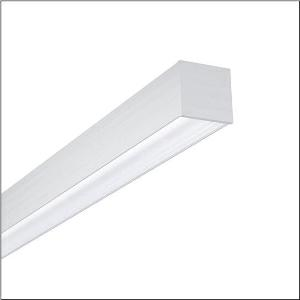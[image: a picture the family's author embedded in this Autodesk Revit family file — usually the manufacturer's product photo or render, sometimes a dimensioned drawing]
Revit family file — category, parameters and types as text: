
# Revit family: silica_r_5mx31bd1e4a_96a8
name_source: partatom
category: Lighting Fixtures
units: mm (PartAtom-declared; Revit-internal decimal feet)

## family parameters
Cut with Voids When Loaded = No
Host = Face
Light Source = No
Part Type = Normal
Room Calculation Point = No
Round Connector Dimension = Use Diameter
Shared = No

## types (1)
- --- (1 x LED, 7070 lm, 45.6 W, 4000K)
    Apparent Load = 46 VA
    CIE Flux Codes = 82 97 100 70 100
    Color Rendering = 80
    Color Temperature = 4000K
    Default Elevation = 1800 mm
    Description = Silica®, office luminaire, of aluminium, light emission: direct/indirect distribution, primary light characteristic: symmetric, installation type: suspended mounting, LED, rated luminous flux: 7.070lm, luminous efficacy: 155lm/W, light colour: 840, colour temperature: 4000K, control gear: ECG DALI, with terminal, 3+2-pole, max. 2.5mm², mains connection: 230V, AC, 50/60Hz, connection cable inclusive, cable length: 1,5m, rated input power: 46W, luminaire housing, of aluminium, anodised, silver, length: 1.442mm, width: 65mm, height: 64mm, protection rating (complete): IP20, insulation class (complete): insulation class I (protective earthing), certification: CE, permissible operating ambient temperature: 0..+35°C, standard: EN 50419, packaging unit: 1 piece
    Height = 64 mm
    Lamp = 1 x LED
    Lamp Light Flux = 7070 lm
    Lamp Power = 45.6 W
    Lamp count = 1
    Length = 1442 mm
    Luminous efficacy = 155 lm/W
    Manufacturer = Siteco
    ModVariant = No
    Model = 5MX31BD1E4A
    Mounting Place = Ceiling
    Mounting Type = Pendant
    Number of Poles = 1
    OnlyDefault = Yes
    Power Factor = 1
    Product Name = Silica®
    Product group = office luminaire | ceiling pendant
    ProductGroupID = 902
    Protection Class = Protection class I
    Protection Degree = IP 20
    RLX_Detail_Level = 1
    RLX_Emergency_Light_Flux = 0 lm
    RLX_Emergency_Type = 0
    RLX_Emergency_Type_DB = No
    RlxData = <blob elided: 32777 chars, md5=91c9da9f>
    Socket = socket
    Standby Power = 0 W
    System Light Flux = 7070 lm
    System Power = 46 W
    Type Comments = factory setting: direct and indirect light
    Type Image = l_1005409.jpg
    URL = http://relux.com
    VarID = @adj_155042
    Voltage = 0 V
    Weight = 0.00 kg
    Width = 66 mm

## geometry (parser evidence)
native form markers: Blend x4, Sweep x12
no freeform markers — native parametric forms only
